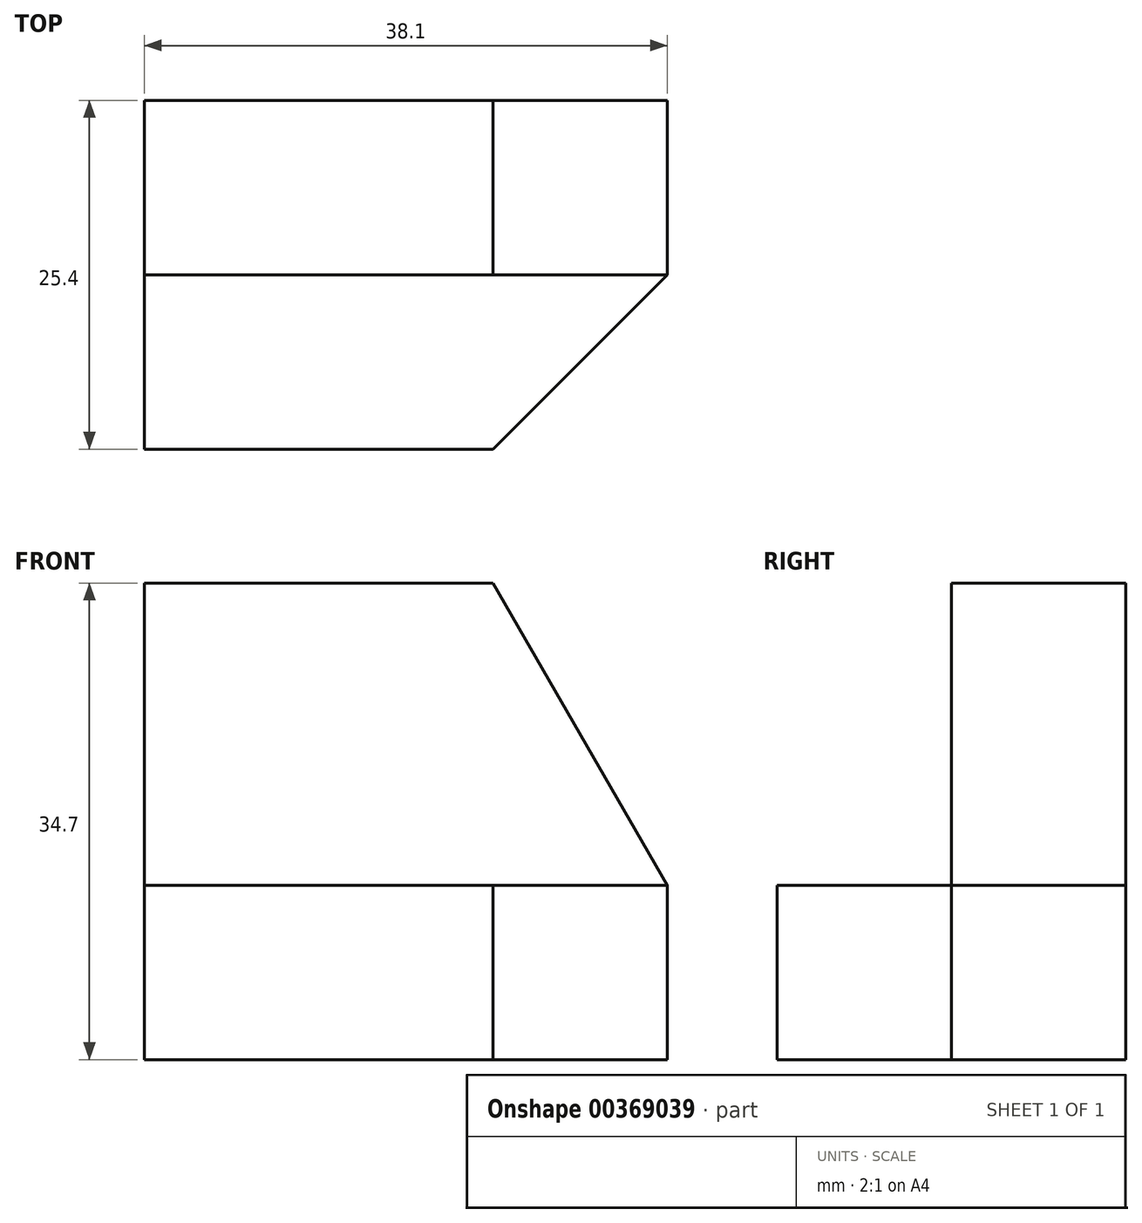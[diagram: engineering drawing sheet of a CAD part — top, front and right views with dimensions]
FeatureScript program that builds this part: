
annotation { "Feature Type Name" : "Feature", "Feature Type Description" : "" }
export const myFeature = defineFeature(function(context is Context, id is Id, definition is map)
    precondition{}
    {
        {
            var Q0;
            Q0=qCreatedBy(makeId("Front.planeOp"),FACE);
            var sketch = newSketch(context, id + "F0", { "sketchPlane" : qUnion([Q0])});
            skLineSegment(sketch, "E0", {"start": v(0, 0) * mm, "end": v(0, 12.7) * mm});
            skLineSegment(sketch, "E1", {"start": v(0, 12.7) * mm, "end": v(-38.1, 12.7) * mm});
            skLineSegment(sketch, "E2", {"start": v(-38.1, 12.7) * mm, "end": v(-38.1, 0) * mm});
            skLineSegment(sketch, "E3", {"start": v(-38.1, 0) * mm, "end": v(0, 0) * mm});
            skSolve(sketch);
        }
        {
            var Q0;
            Q0=makeQuery(id+"F0.imprint","IMPRINT",FACE,{"disambiguationData":[TD([[makeQuery(id+"F0.imprint","IMPRINT",EDGE,{"derivedFrom":sQuery(id+"F0.wireOp",EDGE,"E0")}),1.0]])]});
            extrude(context, id + "F1", {"entities" : qUnion([Q0]), "depth" : 12.7 * mm});
        }
        {
            var Q0;
            Q0=makeQuery(id+"F1.opExtrude","SWEPT_FACE",FACE,{"disambiguationData":[OSD([sQuery(id+"F0.wireOp",EDGE,"E1")])]});
            var sketch = newSketch(context, id + "F2", { "sketchPlane" : qUnion([Q0])});
            skLineSegment(sketch, "E4", {"start": v(0, 0) * mm, "end": v(-12.7, -12.7) * mm});
            skLineSegment(sketch, "E5", {"start": v(-12.7, -12.7) * mm, "end": v(0, -12.7) * mm});
            skLineSegment(sketch, "E6", {"start": v(0, -12.7) * mm, "end": v(0, 0) * mm});
            skSolve(sketch);
        }
        {
            var Q0;
            Q0=makeQuery(id+"F2.imprint","IMPRINT",FACE,{"disambiguationData":[TD([[makeQuery(id+"F2.imprint","IMPRINT",EDGE,{"derivedFrom":sQuery(id+"F2.wireOp",EDGE,"E4")}),1.0]])]});
            extrude(context, id + "F3", {"entities" : qUnion([Q0]), "operationType" : NewBodyOperationType.REMOVE, "oppositeDirection" : true, "depth" : 25.4 * mm});
        }
        {
            var Q0;
            Q0=makeQuery(id+"F1.opExtrude","CAP_FACE",FACE,{"disambiguationData":[OSD([sQuery(id+"F0.wireOp",EDGE,"E0"),sQuery(id+"F0.wireOp",EDGE,"E1"),sQuery(id+"F0.wireOp",EDGE,"E2"),sQuery(id+"F0.wireOp",EDGE,"E3")])],"isStart":true});
            var sketch = newSketch(context, id + "F4", { "sketchPlane" : qUnion([Q0])});
            skLineSegment(sketch, "E7", {"start": v(38.1, 0) * mm, "end": v(38.1, 34.7) * mm});
            skLineSegment(sketch, "E8", {"start": v(38.1, 34.7) * mm, "end": v(12.7, 34.7) * mm});
            skLineSegment(sketch, "E9", {"start": v(12.7, 34.7) * mm, "end": v(0, 12.7) * mm});
            skLineSegment(sketch, "E10", {"start": v(0, 12.7) * mm, "end": v(0, 0) * mm});
            skLineSegment(sketch, "E11", {"start": v(0, 0) * mm, "end": v(38.1, 0) * mm});
            skSolve(sketch);
        }
        {
            var Q0;
            Q0=makeQuery(id+"F4.imprint","IMPRINT",FACE,{"disambiguationData":[TD([[makeQuery(id+"F4.imprint","IMPRINT",EDGE,{"derivedFrom":sQuery(id+"F4.wireOp",EDGE,"E10")}),-1.0]])]});
            var Q1;
            {var subQ2=sQuery(id+"F4.wireOp",EDGE,"E8");Q1=makeQuery(id+"F4.imprint","IMPRINT",FACE,{"disambiguationData":[TD([[makeQuery(id+"F4.imprint","IMPRINT",EDGE,{"derivedFrom":subQ2}),1.0]])]});}
            extrude(context, id + "F5", {"entities" : qUnion([Q0, Q1]), "operationType" : NewBodyOperationType.ADD, "depth" : 12.7 * mm});
        }
    });
